FCSTD DOCUMENT  (FreeCAD 0.19R24276 (Git))
Label: sequence_modeling
License: All rights reserved
LicenseURL: http://en.wikipedia.org/wiki/All_rights_reserved
objects: Sketcher::SketchObject×1, PartDesign::Body×1
note: 2 computed .brp shape members not serialized (recipe doc carries the construction recipe); baked Part::Feature solids carry a one-line shape summary decoded from their .brp

FEATURE [Sketcher::SketchObject] Sketch
  FullyConstrained = false
  MapMode = 5
  Support = -> [XY_Plane]
  sketch-geometry (11):
    g0: LineSegment StartX=80 StartY=-45 StartZ=0 EndX=102.5 EndY=-116.545 EndZ=0
    g1: LineSegment StartX=80 StartY=0 StartZ=0 EndX=125 EndY=0 EndZ=0
    g2: LineSegment StartX=125 StartY=-45 StartZ=0 EndX=102.5 EndY=-116.545 EndZ=0
    g3: LineSegment StartX=125 StartY=0 StartZ=0 EndX=125 EndY=-45 EndZ=0
    g4: LineSegment StartX=223.67 StartY=0 StartZ=0 EndX=223.67 EndY=-45 EndZ=0
    g5: LineSegment StartX=223.67 StartY=-45 StartZ=0 EndX=246.17 EndY=-116.545 EndZ=0
    g6: LineSegment StartX=223.67 StartY=0 StartZ=0 EndX=268.67 EndY=0 EndZ=0
    g7: LineSegment StartX=268.67 StartY=-45 StartZ=0 EndX=246.17 EndY=-116.545 EndZ=0
    g8: LineSegment StartX=268.67 StartY=0 StartZ=0 EndX=268.67 EndY=-45 EndZ=0
    g9: LineSegment StartX=0.459255 StartY=-2e-14 StartZ=0 EndX=29.5818 EndY=-2e-14 EndZ=0
    g10: LineSegment StartX=80 StartY=0 StartZ=0 EndX=80 EndY=-45 EndZ=0
  constraints (30):
    c: DistanceX(g1,g1) = 45
    c: Distance(g0) = 75
    c: DistanceX(g-1,g1) = 80
    c: Tangent(g1,g-1) = -1.5708
    c: Equal(g0,g2) = 75
    c: Coincident(g2,g0)
    c: Coincident(g3,g2)
    c: Coincident(g3,g1)
    c: Equal(g1,g6) = 45
    c: Equal(g0,g5) = 75
    c: Coincident(g4,g6)
    c: Coincident(g5,g4)
    c: Equal(g5,g7) = 75
    c: Equal(g4,g8) = 45
    c: Coincident(g7,g5)
    c: Coincident(g8,g7)
    c: Coincident(g8,g6)
    c: Horizontal(g9)
    c: Coincident(g10,g1)
    c: Coincident(g10,g0)
    c: Parallel(g6,g-1)
    c: PointOnObject(g4,g-1)
    c: DistanceX(g-1,g4) = 223.67
    c: Distance(g10) = 45
    c: Distance(g3) = 45
    c: Distance(g4) = 45
    c: Angle(g9,g10) = 1.5708
    c: Angle(g1,g3) = 1.5708
    c: Angle(g9,g4) = 1.5708
    c: Angle(g6,g8) = 1.5708
FEATURE [PartDesign::Body] Body
  Group = -> [Sketch]
  Origin = -> Origin
